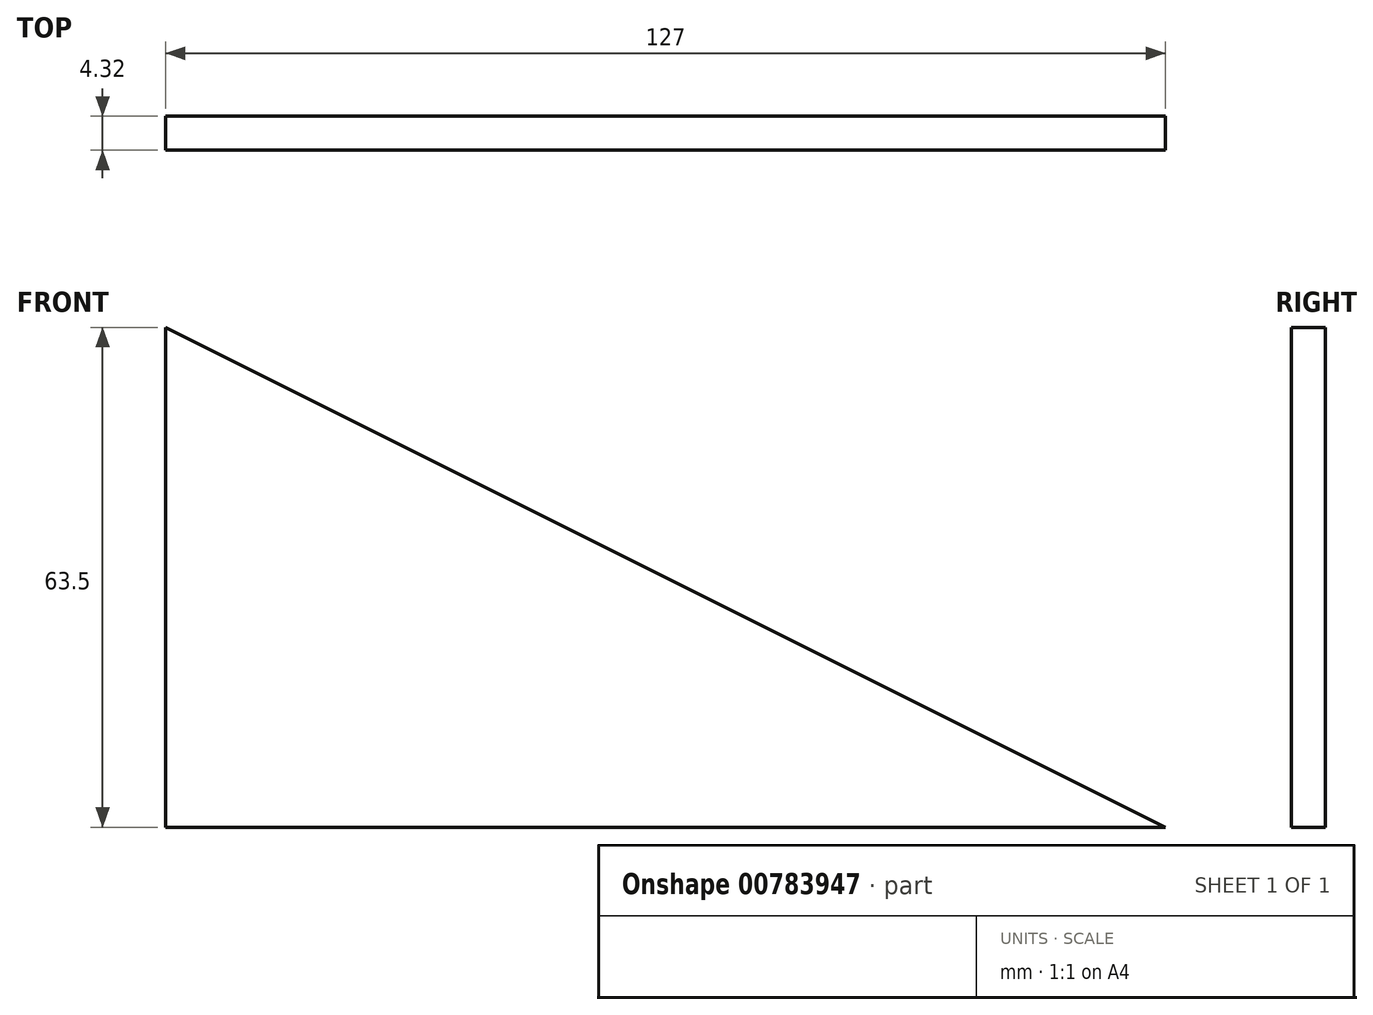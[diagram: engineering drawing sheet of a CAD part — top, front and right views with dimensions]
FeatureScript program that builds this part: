
annotation { "Feature Type Name" : "Feature", "Feature Type Description" : "" }
export const myFeature = defineFeature(function(context is Context, id is Id, definition is map)
    precondition{}
    {
        {
            var Q0;
            Q0=qCreatedBy(makeId("Front.planeOp"),FACE);
            var sketch = newSketch(context, id + "F0", { "sketchPlane" : qUnion([Q0])});
            skLineSegment(sketch, "E0", {"start": v(0, 0) * mm, "end": v(0, 63.5) * mm});
            skLineSegment(sketch, "E1", {"start": v(0, 63.5) * mm, "end": v(127, 0) * mm});
            skLineSegment(sketch, "E2", {"start": v(127, 0) * mm, "end": v(0, 0) * mm});
            skSolve(sketch);
        }
        {
            var Q0;
            Q0 = qSketchRegion(id + "F0", true);
            extrude(context, id + "F1", {"entities" : qUnion([Q0]), "depth" : 4.32 * mm, "offsetDistance" : 25.4 * mm});
        }
    });
